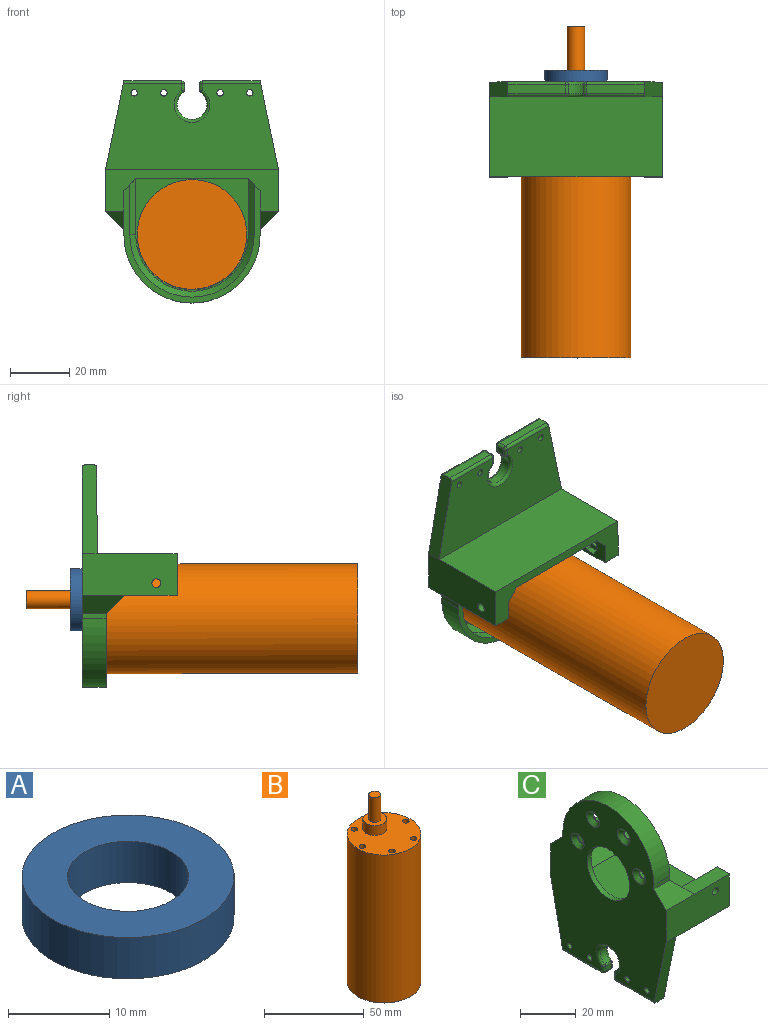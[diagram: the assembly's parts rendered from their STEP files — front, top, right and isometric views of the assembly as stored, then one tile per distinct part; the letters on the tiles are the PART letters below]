
ASSEMBLY  parts=3 mates=3
PART A: 4 faces, bbox 21x21x5 mm
  f0: cylinder r=6mm len=12mm, axis (0,0,-1), area 188.5mm2, adj f2,f3
  f1: cylinder r=10.5mm len=21mm, axis (0,0,-1), area 329.9mm2, adj f2,f3
  f2: plane 21x21mm, normal (0,0,1), area 233.3mm2, adj f0,f1
  f3: plane 21x21mm, normal (0,0,-1), area 233.3mm2, adj f0,f1
PART B: 19 faces, bbox 37x37x112 mm
  f0: cylinder r=18.5mm len=91mm, axis (0,0,-1), area 10577.7mm2, adj f1,f2
  f1: plane 37x37mm, normal (0,0,1), area 913.9mm2, adj f0,f3,f7,f9,f11,f13,f15,f17
  f2: plane 37x37mm, normal (0,0,-1), area 1075.2mm2, adj f0
  f3: cylinder r=6mm len=12mm, axis (0,0,-1), area 226.2mm2, adj f1,f4
  f4: plane 12x12mm, normal (0,0,1), area 84.8mm2, adj f3,f5
  f5: cylinder r=3mm len=15mm, axis (0,0,-1), area 282.7mm2, adj f4,f6
  f6: plane 6x6mm, normal (0,0,1), area 28.3mm2, adj f5
  f7: cylinder r=1.6mm len=5mm, axis (0,0,1), area 50.3mm2, adj f1,f8
  f8: plane 3.2x3.2mm, normal (0,0,1), area 8mm2, adj f7
  f9: cylinder r=1.6mm len=5mm, axis (0,0,1), area 50.3mm2, adj f1,f10
  f10: plane 3.2x3.2mm, normal (0,0,1), area 8mm2, adj f9
  f11: cylinder r=1.6mm len=5mm, axis (0,0,1), area 50.3mm2, adj f1,f12
  f12: plane 3.2x3.2mm, normal (0,0,1), area 8mm2, adj f11
  f13: cylinder r=1.6mm len=5mm, axis (0,0,1), area 50.3mm2, adj f1,f14
  f14: plane 3.2x3.2mm, normal (0,0,1), area 8mm2, adj f13
  f15: cylinder r=1.6mm len=5mm, axis (0,0,1), area 50.3mm2, adj f1,f16
  f16: plane 3.2x3.2mm, normal (0,0,1), area 8mm2, adj f15
  f17: cylinder r=1.6mm len=5mm, axis (0,0,1), area 50.3mm2, adj f1,f18
  f18: plane 3.2x3.2mm, normal (0,0,1), area 8mm2, adj f17
PART C: 86 faces, bbox 32x58.4x75 mm
  f0: cylinder r=1.5mm len=4.2mm, axis (0,-1,0), area 39.6mm2, adj f22,f76
  f1: plane 58.4x27mm, normal (0,0,-1), area 1576.8mm2, adj f21,f22,f27,f45
  f2: plane 8x1.8mm, normal (0,-1,0), area 14.4mm2, adj f9,f11,f15,f28
  f3: plane 8x1.8mm, normal (0,1,0), area 14.4mm2, adj f9,f11,f15,f29
  f4: cylinder r=10.7mm len=21.4mm, axis (-1,0,0), area 134.5mm2, adj f10,f11
  f5: cylinder r=1.6mm len=3.2mm, axis (-1,0,0), area 4mm2, adj f10,f17
  f6: cylinder r=1.6mm len=3.2mm, axis (-1,0,0), area 4mm2, adj f10,f16
  f7: cylinder r=1.6mm len=3.2mm, axis (-1,0,0), area 4mm2, adj f10,f19
  f8: cylinder r=1.6mm len=3.2mm, axis (-1,0,0), area 4mm2, adj f10,f18
  f9: cylinder r=23mm len=46mm, axis (-1,0,0), area 578.1mm2, adj f2,f3,f11,f15
  f10: plane 38x38mm, normal (1,0,0), area 897.2mm2, adj f4,f5,f6,f7,f8,f24,f65,f66
  f11: plane 74x58.4mm, normal (-1,0,0), area 2948.6mm2, adj f2,f3,f4,f9,f16,f17,f18,f19
  f12: plane 17x4mm, normal (0,1,0), area 68mm2, adj f13,f15,f67,f84
  f13: cylinder r=21mm len=42mm, axis (-1,0,0), area 263.9mm2, adj f12,f14,f15,f66
  f14: plane 17x4mm, normal (0,-1,0), area 68mm2, adj f13,f15,f65,f85
  f15: plane 46x40mm, normal (1,0,0), area 202.2mm2, adj f2,f3,f9,f12,f13,f14,f20,f25
  f16: cone r=3.2mm half-angle=45deg, axis (-1,0,0), area 34.1mm2, adj f6,f11
  f17: cone r=3.2mm half-angle=45deg, axis (-1,0,0), area 34.1mm2, adj f5,f11
  f18: cone r=3.2mm half-angle=45deg, axis (-1,0,0), area 34.1mm2, adj f8,f11
  f19: cone r=3.2mm half-angle=45deg, axis (-1,0,0), area 34.1mm2, adj f7,f11
  f20: plane 24x13.2mm, normal (0,-1,0), area 156mm2, adj f15,f23,f27,f68,f70,f72,f73,f74
  f21: plane 32x14mm, normal (0,-1,0), area 440.9mm2, adj f1,f11,f26,f27,f28,f36,f64
  f22: plane 32x14mm, normal (0,1,0), area 440.9mm2, adj f0,f1,f11,f23,f27,f29,f35
  f23: plane 17.8x6.2mm, normal (0,0,1), area 110.4mm2, adj f20,f22,f27,f68
  f24: plane 38x30mm, normal (0,0,1), area 1140mm2, adj f10,f27,f84,f85
  f25: plane 24x13.2mm, normal (0,1,0), area 156mm2, adj f15,f26,f27,f69,f77,f78,f79,f80
  f26: plane 17.8x6.2mm, normal (0,0,1), area 110.4mm2, adj f21,f25,f27,f69
  f27: plane 58.4x14mm, normal (1,0,0), area 327.6mm2, adj f1,f20,f21,f22,f23,f24,f25,f26
  f28: plane 14.2x6.2mm, normal (0,-0.71,0.71), area 97.3mm2, adj f2,f11,f21,f69
  f29: plane 14.2x6.2mm, normal (0,0.71,0.71), area 97.3mm2, adj f3,f11,f22,f68
  f30: cylinder r=5mm len=10mm, axis (-1,0,0), area 75.6mm2, adj f31,f43,f50,f59
  f31: cylinder r=1mm len=3mm, axis (-1,0,0), area 2.8mm2, adj f30,f32,f51,f60
  f32: plane 3x2.13mm, normal (0,-1,0), area 6.4mm2, adj f31,f33,f52,f61
  f33: cylinder r=1mm len=3mm, axis (-1,0,0), area 4.7mm2, adj f32,f34,f53,f62
  f34: plane 19.5x3mm, normal (0,0,-1), area 58.5mm2, adj f33,f35,f54,f63
  f35: plane 30x6.2mm, normal (0,0.98,-0.2), area 152.7mm2, adj f11,f22,f34,f45,f54,f63
  f36: plane 30x6.2mm, normal (0,-0.98,-0.2), area 152.7mm2, adj f11,f21,f37,f45,f46,f55
  f37: plane 19.5x3mm, normal (0,0,-1), area 58.5mm2, adj f36,f38,f46,f55
  f38: cylinder r=1mm len=3mm, axis (-1,0,0), area 4.7mm2, adj f37,f39,f47,f56
  f39: plane 3x2.13mm, normal (0,1,0), area 6.4mm2, adj f38,f43,f48,f57
  f40: cylinder r=1.1mm len=5mm, axis (-1,0,0), area 34.6mm2, adj f11,f45
  f41: cylinder r=1.1mm len=5mm, axis (-1,0,0), area 34.6mm2, adj f11,f45
  f42: cylinder r=1.1mm len=5mm, axis (-1,0,0), area 34.6mm2, adj f11,f45
  f43: cylinder r=1mm len=3mm, axis (-1,0,0), area 2.8mm2, adj f30,f39,f49,f58
  f44: cylinder r=1.1mm len=5mm, axis (-1,0,0), area 34.6mm2, adj f11,f45
  f45: plane 58.4x29mm, normal (1,0,0), area 1382mm2, adj f1,f35,f36,f40,f41,f42,f44,f55
  f46: cylinder r=1mm len=19.71mm, axis (0,1,0), area 30.7mm2, adj f11,f36,f37,f47
  f47: sphere r=1mm, area 1.6mm2, adj f38,f46,f48
  f48: cylinder r=1mm len=2.13mm, axis (0,0,1), area 3.3mm2, adj f11,f39,f47,f49
  f49: sphere r=1mm, area 0.9mm2, adj f43,f48,f50
  f50: torus R=6mm, axis (1,0,0), area 42.4mm2, adj f11,f30,f49,f51
  f51: sphere r=1mm, area 0.9mm2, adj f31,f50,f52
  f52: cylinder r=1mm len=2.13mm, axis (0,0,-1), area 3.3mm2, adj f11,f32,f51,f53
  f53: sphere r=1mm, area 1.6mm2, adj f33,f52,f54
  f54: cylinder r=1mm len=19.71mm, axis (0,1,0), area 30.7mm2, adj f11,f34,f35,f53
  f55: cylinder r=1mm len=19.71mm, axis (0,-1,0), area 30.7mm2, adj f36,f37,f45,f56
  f56: sphere r=1mm, area 1.6mm2, adj f38,f55,f57
  f57: cylinder r=1mm len=2.13mm, axis (0,0,-1), area 3.3mm2, adj f39,f45,f56,f58
  f58: sphere r=1mm, area 0.9mm2, adj f43,f57,f59
  f59: torus R=6mm, axis (1,0,0), area 42.4mm2, adj f30,f45,f58,f60
  f60: sphere r=1mm, area 0.9mm2, adj f31,f59,f61
  f61: cylinder r=1mm len=2.13mm, axis (0,0,1), area 3.3mm2, adj f32,f45,f60,f62
  f62: sphere r=1mm, area 1.6mm2, adj f33,f61,f63
  f63: cylinder r=1mm len=19.71mm, axis (0,-1,0), area 30.7mm2, adj f34,f35,f45,f62
  f64: cylinder r=1.5mm len=4.2mm, axis (0,-1,0), area 39.6mm2, adj f21,f83
  f65: plane 19x2mm, normal (0.71,-0.71,0), area 50.9mm2, adj f10,f14,f66,f85
  f66: cone r=21mm half-angle=45deg, axis (1,0,0), area 177.7mm2, adj f10,f13,f65,f67
  f67: plane 19x2mm, normal (0.71,0.71,0), area 50.9mm2, adj f10,f12,f66,f84
  f68: plane 6.2x6.2mm, normal (0.71,0,0.71), area 27.2mm2, adj f20,f23,f29
  f69: plane 6.2x6.2mm, normal (0.71,0,0.71), area 27.2mm2, adj f25,f26,f28
  f70: plane 3x2mm, normal (-0.87,0,0.5), area 6.9mm2, adj f20,f71,f75,f76
  f71: plane 3.46x2mm, normal (0,0,1), area 6.9mm2, adj f70,f72,f76,f85
  f72: plane 3x2mm, normal (0.87,0,0.5), area 6.9mm2, adj f20,f71,f73,f76
  f73: plane 3x2mm, normal (0.87,0,-0.5), area 6.9mm2, adj f20,f72,f74,f76
  f74: plane 3.46x2mm, normal (0,0,-1), area 6.9mm2, adj f20,f73,f75,f76
  f75: plane 3x2mm, normal (-0.87,0,-0.5), area 6.9mm2, adj f20,f70,f74,f76
  f76: plane 6.93x6mm, normal (0,-1,0), area 24.1mm2, adj f0,f70,f71,f72,f73,f74,f75
  f77: plane 3x2mm, normal (-0.87,0,-0.5), area 6.9mm2, adj f25,f78,f82,f83
  f78: plane 3.46x2mm, normal (0,0,-1), area 6.9mm2, adj f25,f77,f79,f83
  f79: plane 3x2mm, normal (0.87,0,-0.5), area 6.9mm2, adj f25,f78,f80,f83
  f80: plane 3x2mm, normal (0.87,0,0.5), area 6.9mm2, adj f25,f79,f81,f83
  f81: plane 3.46x2mm, normal (0,0,1), area 6.9mm2, adj f80,f82,f83,f84
  f82: plane 3x2mm, normal (-0.87,0,0.5), area 6.9mm2, adj f25,f77,f81,f83
  f83: plane 6.93x6mm, normal (0,1,0), area 24.1mm2, adj f64,f77,f78,f79,f80,f81,f82
  f84: plane 30x4mm, normal (0,0.71,0.71), area 149.9mm2, adj f12,f15,f24,f25,f27,f67,f81
  f85: plane 30x4mm, normal (0,-0.71,0.71), area 149.9mm2, adj f14,f15,f20,f24,f27,f65,f71
PLACE A rot(axis=(0,-0.71,-0.71),180deg) t=(-12.79,-31.89,-0.27)mm
PLACE B rot(axis=(0,0.71,0.71),180deg) t=(-12.79,-123.9,-6.59)mm
PLACE C rot(axis=(0.71,-0.71,0),179.9deg) t=(-12.79,-30.9,-6.77)mm
MATE fastened B.f3 <-> A.f1  axis (0,1,0) through (-12.79,-26.89,-0.28)mm
MATE fastened C.f8 <-> B.f7  axis (0,-1,0) through (-5.04,-32.93,-20.19)mm
MATE fastened B.f11 <-> C.f6  axis (0,1,0) through (-28.29,-32.9,-6.77)mm
